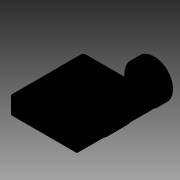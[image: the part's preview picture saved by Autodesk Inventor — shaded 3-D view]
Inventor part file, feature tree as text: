
AUTODESK INVENTOR PART (.ipt)
format: ipt  version: 2014 SP2 (Build 180246200, 246)  size: 214,016 bytes
history: native  units: in
note: dims shown in document units (in); Inventor stores cm internally (conversion verified against a paired STEP export)
features: other x35, sketch x9, extrude x7, revolve x2
ambient origin geometry x8: Origin, YZ Plane, XZ Plane, XY Plane, X Axis, Y Axis, Z Axis, Center Point
bodies: Solid1 (feature_tree)
feature tree (53):
  extrude  "Extrusion1"  Depth=1.5748in TaperAngle=0.0deg
  extrude  "Extrusion2"  Depth=1.5748in TaperAngle=0.0deg
  extrude  "Extrusion3"  TaperAngle=360.0deg  [1 undecoded]
  extrude  "Extrusion4"  TaperAngle=360.0deg  [1 undecoded]
  extrude  "Extrusion5"  [1 undecoded]
  revolve  "Revolution1"  [1 undecoded]
  extrude  "Extrusion6"  [1 undecoded]
  revolve  "Revolution2"  [1 undecoded]
  extrude  "Extrusion7"  [1 undecoded]
  other  "to_b_XY"
  other  "to_b_YZ"
  other  "to_b_ZX"
  other  "to_b_X"
  other  "to_b_Y"
  other  "to_b_Z"
  other  "to_b_Center"
  other  "to_pin_XY"
  other  "to_pin_YZ"
  other  "to_pin_ZX"
  other  "to_pin_X"
  other  "to_pin_Y"
  other  "to_pin_Z"
  other  "to_pin_Center"
  other  "to_washer1_XY"
  other  "to_washer1_YZ"
  other  "to_washer1_ZX"
  other  "to_washer1_X"
  other  "to_washer1_Y"
  other  "to_washer1_Z"
  other  "to_washer1_Center"
  other  "to_washer2_XY"
  other  "to_washer2_YZ"
  other  "to_washer2_ZX"
  other  "to_washer2_X"
  other  "to_washer2_Y"
  other  "to_washer2_Z"
  other  "to_washer2_Center"
  other  "to_washer3_XY"
  other  "to_washer3_YZ"
  other  "to_washer3_ZX"
  other  "to_washer3_X"
  other  "to_washer3_Y"
  other  "to_washer3_Z"
  other  "to_washer3_Center"
  sketch  "Sketch_1"  dims[d0=0.312in d1=0.0in d2=1.5748in d3=0.0in]
  sketch  "Sketch_2"  dims[d4=2.9134in d5=0.0in d6=1.5748in d7=0.0in]
  sketch  "Sketch_3"  dims[d8=0.462in d9=0.0in d10=360.0deg]
  sketch  "Sketch_4"  dims[d11=0.462in d12=0.0in d13=360.0deg]
  sketch  "Sketch_5"  dims[d14=1.5748in d15=0.0in]
  sketch  "Sketch_6"
  sketch  "Sketch_7"
  sketch  "Sketch_8"
  sketch  "Sketch_9"
note: 7 required parameter values undecoded (feature->parameter linkage not recoverable at this tier; creation-order binding heuristic only, values carry confidence <= 0.55)
